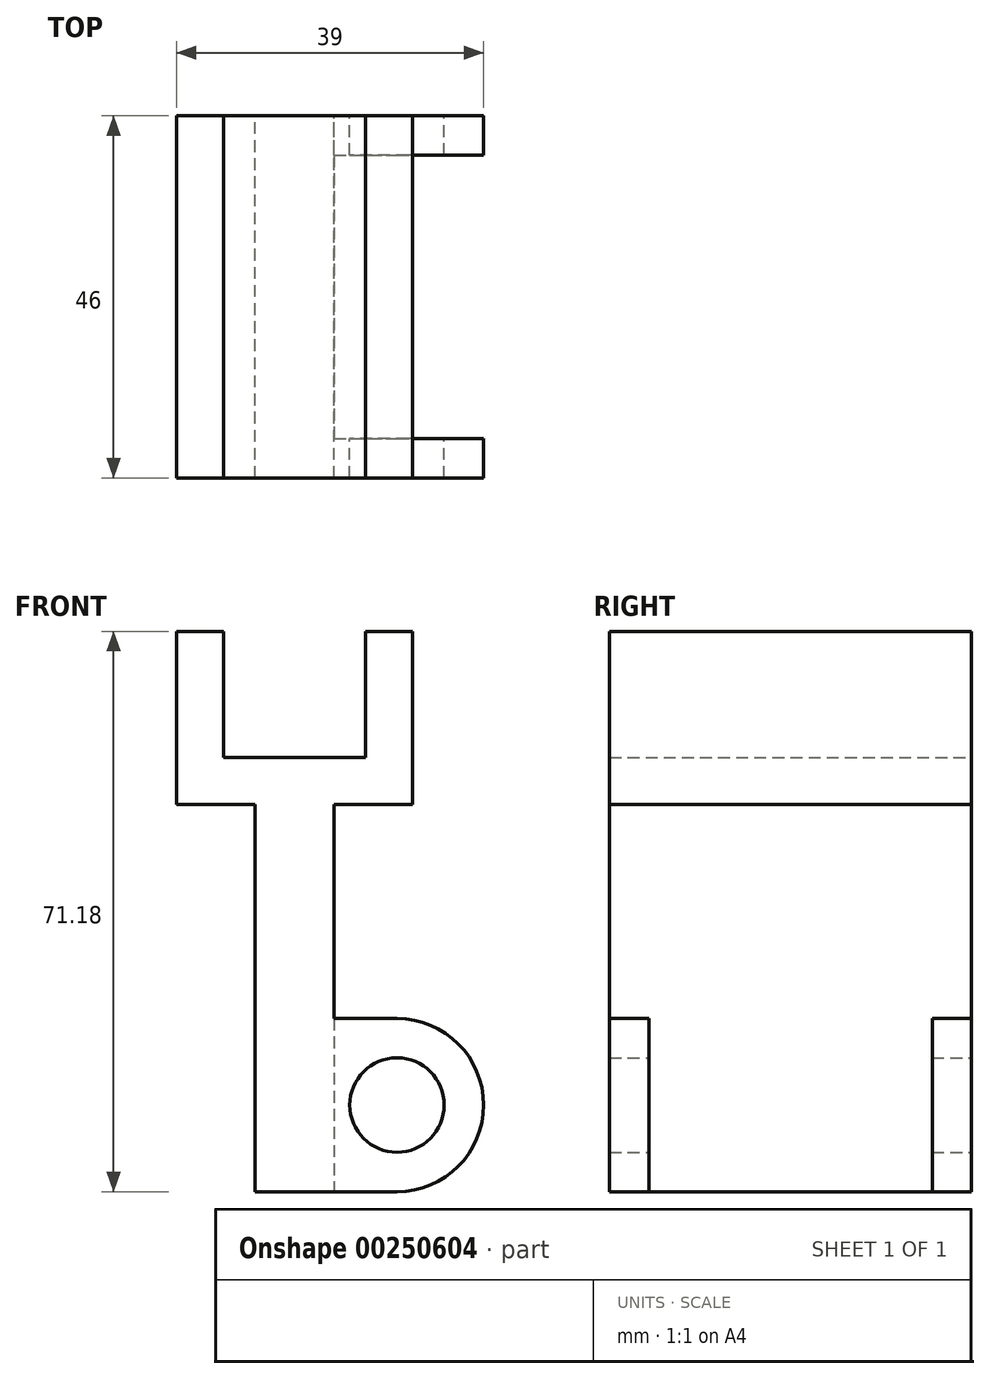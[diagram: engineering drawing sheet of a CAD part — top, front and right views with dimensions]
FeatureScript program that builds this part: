
annotation { "Feature Type Name" : "Feature", "Feature Type Description" : "" }
export const myFeature = defineFeature(function(context is Context, id is Id, definition is map)
    precondition{}
    {
        {
            var Q0;
            Q0=qCreatedBy(makeId("Front.planeOp"),FACE);
            var sketch = newSketch(context, id + "F0", { "sketchPlane" : qUnion([Q0])});
            skLineSegment(sketch, "E0", {"start": v(-15, 45) * mm, "end": v(-15, 23) * mm});
            skLineSegment(sketch, "E1", {"start": v(-15, 23) * mm, "end": v(-5, 23) * mm});
            skLineSegment(sketch, "E2", {"start": v(-5, 23) * mm, "end": v(-5, -26.18) * mm});
            skLineSegment(sketch, "E3", {"start": v(-5, -26.18) * mm, "end": v(5, -26.18) * mm});
            skLineSegment(sketch, "E4", {"start": v(5, -4.18) * mm, "end": v(5, 23) * mm});
            skLineSegment(sketch, "E5", {"start": v(5, 23) * mm, "end": v(15, 23) * mm});
            skLineSegment(sketch, "E6", {"start": v(15, 23) * mm, "end": v(15, 45) * mm});
            skLineSegment(sketch, "E7", {"start": v(15, 45) * mm, "end": v(9, 45) * mm});
            skLineSegment(sketch, "E8", {"start": v(9, 45) * mm, "end": v(9, 29) * mm});
            skLineSegment(sketch, "E9", {"start": v(9, 29) * mm, "end": v(-9, 29) * mm});
            skLineSegment(sketch, "E10", {"start": v(-9, 29) * mm, "end": v(-9, 45) * mm});
            skLineSegment(sketch, "E11", {"start": v(-9, 45) * mm, "end": v(-15, 45) * mm});
            skLineSegment(sketch, "E12", {"start": v(5, -26.18) * mm, "end": v(13, -26.18) * mm});
            skLineSegment(sketch, "E13", {"start": v(13, -4.18) * mm, "end": v(5, -4.18) * mm});
            skArc(sketch, "E14", {"start": v(13, -26.18) * mm, "mid": v(24, -15.18) * mm, "end": v(13, -4.18) * mm});
            skCircle(sketch, "E15", {"center": v(13, -15.18) * mm, "radius": 6 * mm});
            skSolve(sketch);
        }
        {
            var Q0;
            Q0 = qSketchRegion(id + "F0", true);
            extrude(context, id + "F1", {"entities" : qUnion([Q0]), "depth" : 46 * mm});
        }
        {
            var Q0;
            Q0=makeQuery(id+"F1.opExtrude","SWEPT_FACE",FACE,{"disambiguationData":[OSD([sQuery(id+"F0.wireOp",EDGE,"E3"),sQuery(id+"F0.wireOp",EDGE,"E12")])]});
            var sketch = newSketch(context, id + "F2", { "sketchPlane" : qUnion([Q0])});
            skLineSegment(sketch, "E16.bottom", {"start": v(5, 5) * mm, "end": v(31.92, 5) * mm});
            skLineSegment(sketch, "E16.top", {"start": v(5, 41) * mm, "end": v(31.92, 41) * mm});
            skLineSegment(sketch, "E16.left", {"start": v(5, 5) * mm, "end": v(5, 41) * mm});
            skLineSegment(sketch, "E16.right", {"start": v(31.92, 5) * mm, "end": v(31.92, 41) * mm});
            skSolve(sketch);
        }
        {
            var Q0;
            Q0 = qSketchRegion(id + "F2", true);
            extrude(context, id + "F3", {"entities" : qUnion([Q0]), "oppositeDirection" : true, "depth" : 42.5 * mm});
        }
        {
            var Q0;
            Q0=makeQuery(id+"F3.opExtrude","SWEPT_BODY",BODY,{"disambiguationData":[OSD([sQuery(id+"F2.wireOp",EDGE,"E16.bottom"),sQuery(id+"F2.wireOp",EDGE,"E16.top"),sQuery(id+"F2.wireOp",EDGE,"E16.left"),sQuery(id+"F2.wireOp",EDGE,"E16.right")])]});
            var Q1;
            Q1=makeQuery(id+"F1.opExtrude","SWEPT_BODY",BODY,{"disambiguationData":[OSD([sQuery(id+"F0.wireOp",EDGE,"E0"),sQuery(id+"F0.wireOp",EDGE,"E1"),sQuery(id+"F0.wireOp",EDGE,"E2"),sQuery(id+"F0.wireOp",EDGE,"E3"),sQuery(id+"F0.wireOp",EDGE,"E4"),sQuery(id+"F0.wireOp",EDGE,"E5"),sQuery(id+"F0.wireOp",EDGE,"E6"),sQuery(id+"F0.wireOp",EDGE,"E7"),sQuery(id+"F0.wireOp",EDGE,"E8"),sQuery(id+"F0.wireOp",EDGE,"E9"),sQuery(id+"F0.wireOp",EDGE,"E10"),sQuery(id+"F0.wireOp",EDGE,"E11"),sQuery(id+"F0.wireOp",EDGE,"E12"),sQuery(id+"F0.wireOp",EDGE,"E13"),sQuery(id+"F0.wireOp",EDGE,"E14"),sQuery(id+"F0.wireOp",EDGE,"E15")])]});
            booleanBodies(context, id + "F4", {"operationType" : BooleanOperationType.SUBTRACTION, "tools" : qUnion([Q0]), "targets" : qUnion([Q1])});
        }
    });
